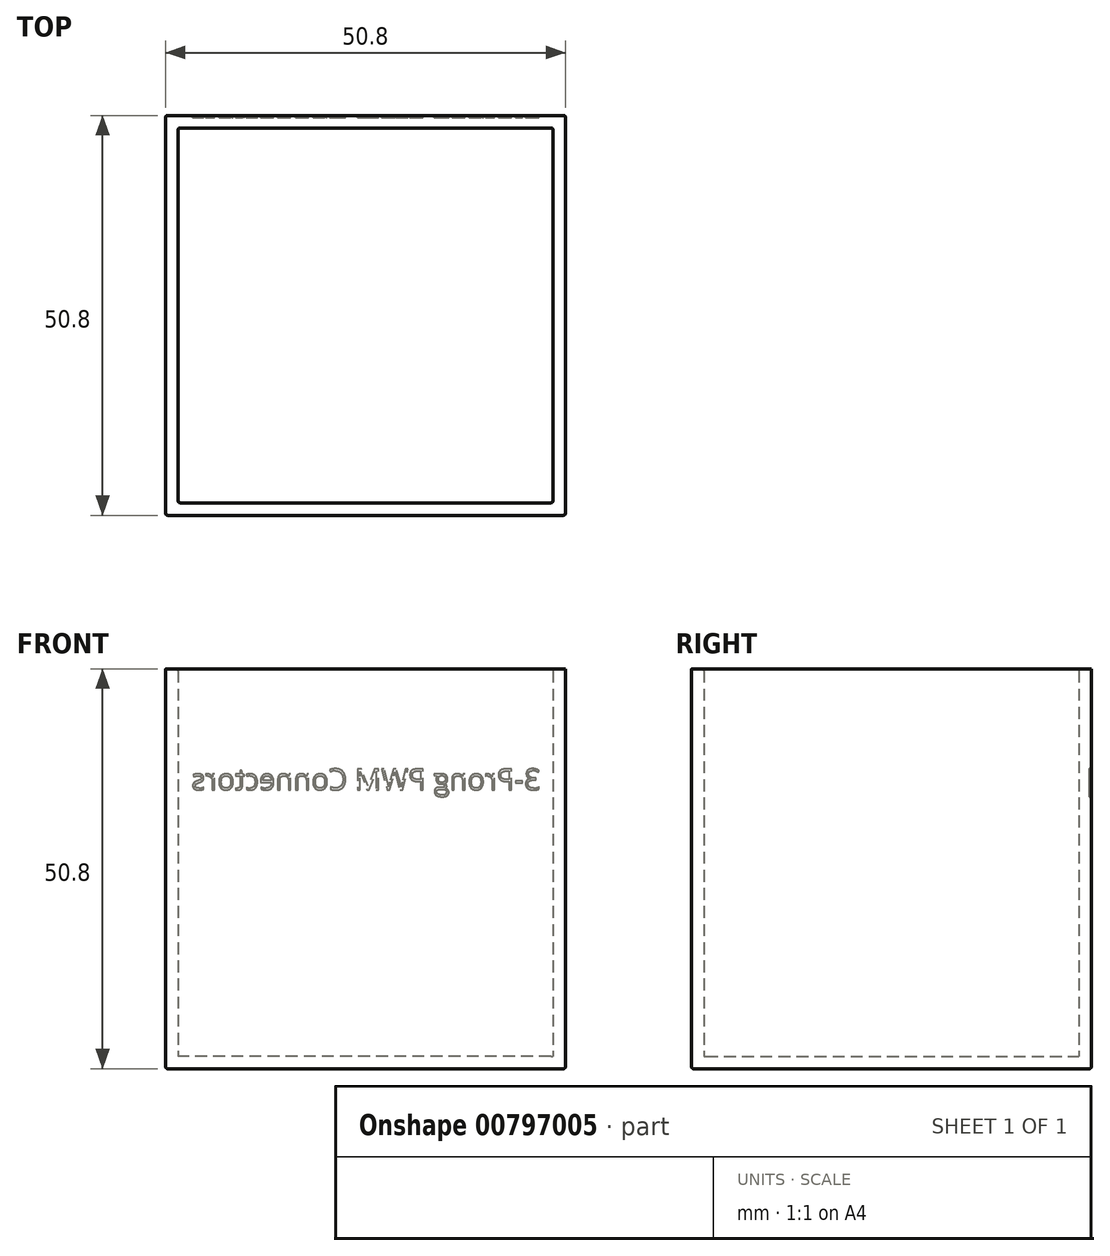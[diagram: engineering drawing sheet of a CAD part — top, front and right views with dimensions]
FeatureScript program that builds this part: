
annotation { "Feature Type Name" : "Feature", "Feature Type Description" : "" }
export const myFeature = defineFeature(function(context is Context, id is Id, definition is map)
    precondition{}
    {
        {
            var Q0;
            Q0=qCreatedBy(makeId("Top.planeOp"),FACE);
            var sketch = newSketch(context, id + "F0", { "sketchPlane" : qUnion([Q0])});
            skLineSegment(sketch, "E0.bottom", {"start": v(25.4, -25.4) * mm, "end": v(-25.4, -25.4) * mm});
            skLineSegment(sketch, "E0.top", {"start": v(25.4, 25.4) * mm, "end": v(-25.4, 25.4) * mm});
            skLineSegment(sketch, "E0.left", {"start": v(25.4, -25.4) * mm, "end": v(25.4, 25.4) * mm});
            skLineSegment(sketch, "E0.right", {"start": v(-25.4, -25.4) * mm, "end": v(-25.4, 25.4) * mm});
            skPoint(sketch, "E0.middle", {"position": v(0, 0) * mm});
            skSolve(sketch);
        }
        {
            var Q0;
            Q0=qSketchRegion(id+"F0",true);
            extrude(context, id + "F1", {"entities" : qUnion([Q0]), "depth" : 1.59 * mm, "offsetDistance" : 25.4 * mm});
        }
        {
            var Q0;
            Q0=makeQuery(id+"F1.opExtrude","CAP_FACE",FACE,{"disambiguationData":[OSD([sQuery(id+"F0.wireOp",EDGE,"E0.bottom"),sQuery(id+"F0.wireOp",EDGE,"E0.top"),sQuery(id+"F0.wireOp",EDGE,"E0.left"),sQuery(id+"F0.wireOp",EDGE,"E0.right")])],"isStart":false});
            var sketch = newSketch(context, id + "F2", { "sketchPlane" : qUnion([Q0])});
            skLineSegment(sketch, "E1.bottom", {"start": v(25.4, -25.4) * mm, "end": v(-25.4, -25.4) * mm});
            skLineSegment(sketch, "E1.top", {"start": v(25.4, 25.4) * mm, "end": v(-25.4, 25.4) * mm});
            skLineSegment(sketch, "E1.left", {"start": v(25.4, -25.4) * mm, "end": v(25.4, 25.4) * mm});
            skLineSegment(sketch, "E1.right", {"start": v(-25.4, -25.4) * mm, "end": v(-25.4, 25.4) * mm});
            skPoint(sketch, "E1.middle", {"position": v(0, 0) * mm});
            skLineSegment(sketch, "E2.0", {"start": v(23.81, 23.81) * mm, "end": v(-23.81, 23.81) * mm});
            skLineSegment(sketch, "E2.1", {"start": v(23.81, -23.81) * mm, "end": v(23.81, 23.81) * mm});
            skLineSegment(sketch, "E2.2", {"start": v(23.81, -23.81) * mm, "end": v(-23.81, -23.81) * mm});
            skLineSegment(sketch, "E2.3", {"start": v(-23.81, -23.81) * mm, "end": v(-23.81, 23.81) * mm});
            skSolve(sketch);
        }
        {
            var Q0;
            Q0=qSketchRegion(id+"F2",true);
            extrude(context, id + "F3", {"entities" : qUnion([Q0]), "operationType" : NewBodyOperationType.ADD, "depth" : 49.2 * mm, "offsetDistance" : 25.4 * mm});
        }
        {
            var Q0;
            Q0=makeQuery(id+"F3.opExtrude","CAP_EDGE",EDGE,{"disambiguationData":[OSD([sQuery(id+"F2.wireOp",EDGE,"E2.3")])],"isStart":true});
            var Q1;
            Q1=makeQuery(id+"F3.opExtrude","SWEPT_EDGE",EDGE,{"disambiguationData":[OSD([sQuery(id+"F2.wireOp",EDGE,"E2.2"),sQuery(id+"F2.wireOp",EDGE,"E2.3")])]});
            var Q2;
            Q2=makeQuery(id+"F3.opExtrude","CAP_EDGE",EDGE,{"disambiguationData":[OSD([sQuery(id+"F2.wireOp",EDGE,"E2.2")])],"isStart":true});
            var Q3;
            Q3=makeQuery(id+"F3.opExtrude","CAP_EDGE",EDGE,{"disambiguationData":[OSD([sQuery(id+"F2.wireOp",EDGE,"E2.3")])],"isStart":false});
            var Q4;
            Q4=makeQuery(id+"F3.opExtrude","CAP_EDGE",EDGE,{"disambiguationData":[OSD([sQuery(id+"F2.wireOp",EDGE,"E2.2")])],"isStart":false});
            var Q5;
            Q5=makeQuery(id+"F3.opExtrude","CAP_EDGE",EDGE,{"disambiguationData":[OSD([sQuery(id+"F2.wireOp",EDGE,"E2.0")])],"isStart":true});
            var Q6;
            Q6=makeQuery(id+"F3.opExtrude","SWEPT_EDGE",EDGE,{"disambiguationData":[OSD([sQuery(id+"F2.wireOp",EDGE,"E2.0"),sQuery(id+"F2.wireOp",EDGE,"E2.3")])]});
            var Q7;
            Q7=makeQuery(id+"F3.opExtrude","CAP_EDGE",EDGE,{"disambiguationData":[OSD([sQuery(id+"F2.wireOp",EDGE,"E2.0")])],"isStart":false});
            var Q8;
            Q8=makeQuery(id+"F3.opExtrude","SWEPT_EDGE",EDGE,{"disambiguationData":[OSD([sQuery(id+"F2.wireOp",EDGE,"E2.0"),sQuery(id+"F2.wireOp",EDGE,"E2.1")])]});
            var Q9;
            Q9=makeQuery(id+"F3.opExtrude","CAP_EDGE",EDGE,{"disambiguationData":[OSD([sQuery(id+"F2.wireOp",EDGE,"E2.1")])],"isStart":true});
            var Q10;
            Q10=makeQuery(id+"F3.opExtrude","CAP_EDGE",EDGE,{"disambiguationData":[OSD([sQuery(id+"F2.wireOp",EDGE,"E2.1")])],"isStart":false});
            var Q11;
            Q11=makeQuery(id+"F3.opExtrude","SWEPT_EDGE",EDGE,{"disambiguationData":[OSD([sQuery(id+"F2.wireOp",EDGE,"E2.1"),sQuery(id+"F2.wireOp",EDGE,"E2.2")])]});
            var Q12;
            Q12=makeQuery(id+"F3.boolean.opBoolean","MERGE",EDGE,{"derivedFrom":[makeQuery(id+"F1.opExtrude","SWEPT_EDGE",EDGE,{"disambiguationData":[OSD([sQuery(id+"F0.wireOp",EDGE,"E0.bottom"),sQuery(id+"F0.wireOp",EDGE,"E0.right")])]}),makeQuery(id+"F3.opExtrude","SWEPT_EDGE",EDGE,{"disambiguationData":[OSD([sQuery(id+"F2.wireOp",EDGE,"E1.bottom"),sQuery(id+"F2.wireOp",EDGE,"E1.right")])]})]});
            var Q13;
            Q13=makeQuery(id+"F3.boolean.opBoolean","MERGE",EDGE,{"derivedFrom":[makeQuery(id+"F1.opExtrude","SWEPT_EDGE",EDGE,{"disambiguationData":[OSD([sQuery(id+"F0.wireOp",EDGE,"E0.bottom"),sQuery(id+"F0.wireOp",EDGE,"E0.left")])]}),makeQuery(id+"F3.opExtrude","SWEPT_EDGE",EDGE,{"disambiguationData":[OSD([sQuery(id+"F2.wireOp",EDGE,"E1.bottom"),sQuery(id+"F2.wireOp",EDGE,"E1.left")])]})]});
            var Q14;
            Q14=makeQuery(id+"F3.boolean.opBoolean","MERGE",EDGE,{"derivedFrom":[makeQuery(id+"F1.opExtrude","SWEPT_EDGE",EDGE,{"disambiguationData":[OSD([sQuery(id+"F0.wireOp",EDGE,"E0.top"),sQuery(id+"F0.wireOp",EDGE,"E0.left")])]}),makeQuery(id+"F3.opExtrude","SWEPT_EDGE",EDGE,{"disambiguationData":[OSD([sQuery(id+"F2.wireOp",EDGE,"E1.top"),sQuery(id+"F2.wireOp",EDGE,"E1.left")])]})]});
            var Q15;
            Q15=makeQuery(id+"F3.boolean.opBoolean","MERGE",EDGE,{"derivedFrom":[makeQuery(id+"F1.opExtrude","SWEPT_EDGE",EDGE,{"disambiguationData":[OSD([sQuery(id+"F0.wireOp",EDGE,"E0.top"),sQuery(id+"F0.wireOp",EDGE,"E0.right")])]}),makeQuery(id+"F3.opExtrude","SWEPT_EDGE",EDGE,{"disambiguationData":[OSD([sQuery(id+"F2.wireOp",EDGE,"E1.top"),sQuery(id+"F2.wireOp",EDGE,"E1.right")])]})]});
            var Q16;
            Q16=makeQuery(id+"F1.opExtrude","CAP_EDGE",EDGE,{"disambiguationData":[OSD([sQuery(id+"F0.wireOp",EDGE,"E0.right")])],"isStart":true});
            var Q17;
            Q17=makeQuery(id+"F1.opExtrude","CAP_EDGE",EDGE,{"disambiguationData":[OSD([sQuery(id+"F0.wireOp",EDGE,"E0.bottom")])],"isStart":true});
            var Q18;
            Q18=makeQuery(id+"F1.opExtrude","CAP_EDGE",EDGE,{"disambiguationData":[OSD([sQuery(id+"F0.wireOp",EDGE,"E0.top")])],"isStart":true});
            var Q19;
            Q19=makeQuery(id+"F1.opExtrude","CAP_EDGE",EDGE,{"disambiguationData":[OSD([sQuery(id+"F0.wireOp",EDGE,"E0.left")])],"isStart":true});
            fillet(context, id + "F4", {"entities" : qUnion([Q0, Q1, Q2, Q3, Q4, Q5, Q6, Q7, Q8, Q9, Q10, Q11, Q12, Q13, Q14, Q15, Q16, Q17, Q18, Q19]), "radius" : 0.25 * mm, "tangentPropagation" : true, "allowEdgeOverflow" : false});
        }
        {
            var Q0;
            Q0=makeQuery(id+"F3.boolean.opBoolean","MERGE",FACE,{"derivedFrom":[makeQuery(id+"F1.opExtrude","SWEPT_FACE",FACE,{"disambiguationData":[OSD([sQuery(id+"F0.wireOp",EDGE,"E0.top")])]}),makeQuery(id+"F3.opExtrude","SWEPT_FACE",FACE,{"disambiguationData":[OSD([sQuery(id+"F2.wireOp",EDGE,"E1.top")])]})]});
            var sketch = newSketch(context, id + "F5", { "sketchPlane" : qUnion([Q0])});
            skText(sketch, "E3", { "text": "3-Prong PWM Connectors", "fontName": "OpenSans-Regular.ttf"});
            const initialGuessF5  = {"E3": [-0.02223, 0.03543, 1, 0, 0.00267]};
            skSetInitialGuess(sketch, initialGuessF5);
            skSolve(sketch);
        }
        {
            var Q0;
            Q0 = qSketchRegion(id + "F5", true);
            extrude(context, id + "F6", {"entities" : qUnion([Q0]), "operationType" : NewBodyOperationType.REMOVE, "oppositeDirection" : true, "depth" : 0.25 * mm, "offsetDistance" : 25.4 * mm});
        }
    });
